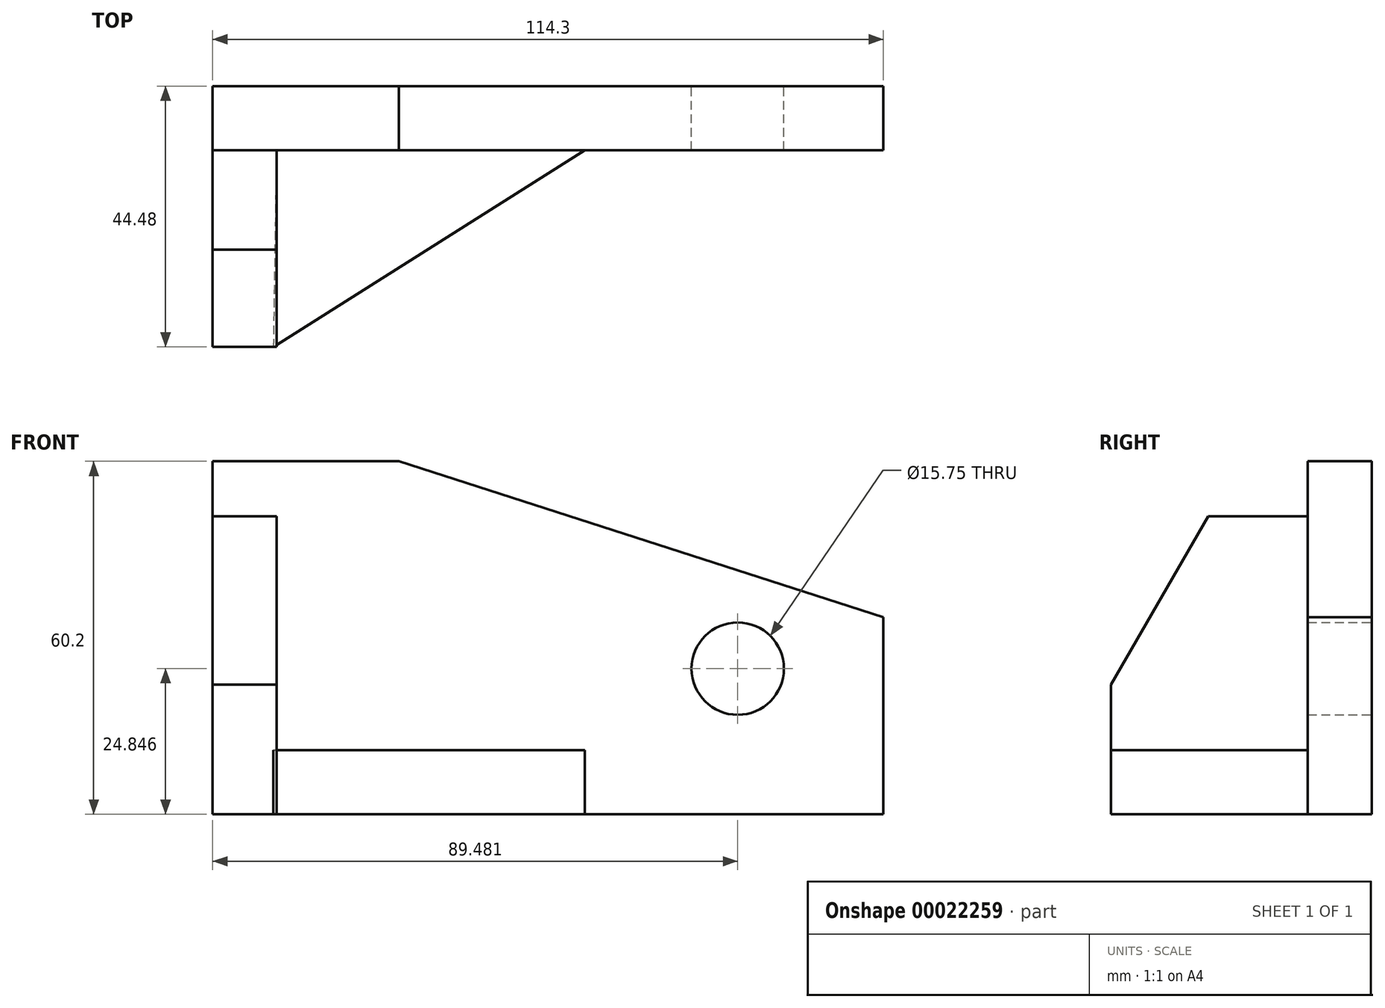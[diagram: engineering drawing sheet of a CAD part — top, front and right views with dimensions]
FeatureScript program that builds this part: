
annotation { "Feature Type Name" : "Feature", "Feature Type Description" : "" }
export const myFeature = defineFeature(function(context is Context, id is Id, definition is map)
    precondition{}
    {
        {
            var Q0;
            Q0=qCreatedBy(makeId("Front.planeOp"),FACE);
            var sketch = newSketch(context, id + "F0", { "sketchPlane" : qUnion([Q0])});
            skLineSegment(sketch, "E0.bottom", {"start": v(-58.5, 21.2) * mm, "end": v(-26.74, 21.2) * mm});
            skLineSegment(sketch, "E0.top", {"start": v(-58.5, -39) * mm, "end": v(55.8, -39) * mm});
            skLineSegment(sketch, "E0.left", {"start": v(-58.5, 21.2) * mm, "end": v(-58.5, -39) * mm});
            skLineSegment(sketch, "E0.right", {"start": v(55.8, -5.37) * mm, "end": v(55.8, -39) * mm});
            skLineSegment(sketch, "E1", {"start": v(-26.74, 21.2) * mm, "end": v(55.8, -5.37) * mm});
            skCircle(sketch, "E2", {"center": v(31, -14.15) * mm, "radius": 7.87 * mm});
            skSolve(sketch);
        }
        {
            var Q0;
            Q0=makeQuery(id+"F0.imprint","IMPRINT",FACE,{"disambiguationData":[TD([[makeQuery(id+"F0.imprint","IMPRINT",EDGE,{"derivedFrom":sQuery(id+"F0.wireOp",EDGE,"E0.bottom")}),-1.0]])]});
            extrude(context, id + "F1", {"entities" : qUnion([Q0]), "depth" : 10.92 * mm});
        }
        {
            var Q0;
            Q0=makeQuery(id+"F1.opExtrude","SWEPT_FACE",FACE,{"disambiguationData":[OSD([sQuery(id+"F0.wireOp",EDGE,"E0.left")])]});
            var sketch = newSketch(context, id + "F2", { "sketchPlane" : qUnion([Q0])});
            skLineSegment(sketch, "E3.bottom", {"start": v(10.92, -39) * mm, "end": v(44.45, -39) * mm});
            skLineSegment(sketch, "E3.top", {"start": v(10.92, 11.8) * mm, "end": v(27.88, 11.8) * mm});
            skLineSegment(sketch, "E3.left", {"start": v(10.92, -39) * mm, "end": v(10.92, 11.8) * mm});
            skLineSegment(sketch, "E3.right", {"start": v(44.45, -39) * mm, "end": v(44.45, -16.9) * mm});
            skLineSegment(sketch, "E4", {"start": v(27.88, 11.8) * mm, "end": v(44.45, -16.9) * mm});
            skPoint(sketch, "E5.orphan", {"position": v(44.45, 11.8) * mm});
            skSolve(sketch);
        }
        {
            var Q0;
            Q0=makeQuery(id+"F2.imprint","IMPRINT",FACE,{"disambiguationData":[TD([[makeQuery(id+"F2.imprint","IMPRINT",EDGE,{"derivedFrom":sQuery(id+"F2.wireOp",EDGE,"E3.bottom")}),1.0]])]});
            extrude(context, id + "F3", {"entities" : qUnion([Q0]), "oppositeDirection" : true, "depth" : 10.92 * mm});
        }
        {
            var Q0;
            Q0=makeQuery(id+"F1.opExtrude","SWEPT_FACE",FACE,{"disambiguationData":[OSD([sQuery(id+"F0.wireOp",EDGE,"E0.top")])]});
            var sketch = newSketch(context, id + "F4", { "sketchPlane" : qUnion([Q0])});
            skLineSegment(sketch, "E6.bottom", {"start": v(-47.63, 10.92) * mm, "end": v(4.95, 10.92) * mm});
            skLineSegment(sketch, "E6.left", {"start": v(-47.63, 10.92) * mm, "end": v(-48.13, 44.48) * mm});
            skLineSegment(sketch, "E7", {"start": v(-48.13, 44.48) * mm, "end": v(4.95, 10.92) * mm});
            skSolve(sketch);
        }
        {
            var Q0;
            Q0=makeQuery(id+"F4.imprint","IMPRINT",FACE,{"disambiguationData":[TD([[makeQuery(id+"F4.imprint","IMPRINT",EDGE,{"derivedFrom":sQuery(id+"F4.wireOp",EDGE,"E6.bottom")}),1.0]])]});
            extrude(context, id + "F5", {"entities" : qUnion([Q0]), "oppositeDirection" : true, "depth" : 10.92 * mm});
        }
    });
